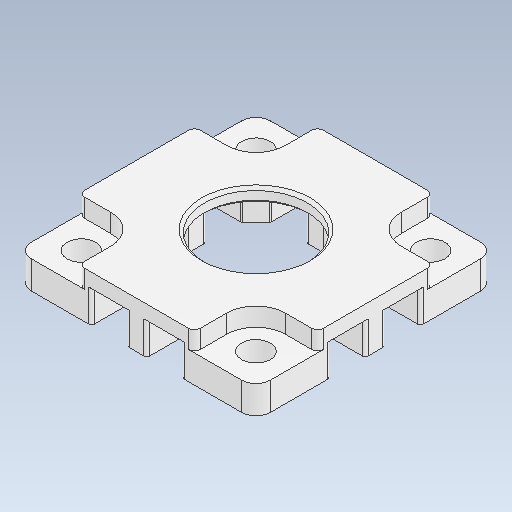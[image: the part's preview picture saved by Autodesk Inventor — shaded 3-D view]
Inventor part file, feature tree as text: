
AUTODESK INVENTOR PART (.ipt)
format: ipt  version: 2020 (Build 240168000, 168)  size: 182,784 bytes
history: native  units: in
note: dims shown in document units (in); Inventor stores cm internally (conversion verified against a paired STEP export)
features: fillet x1
ambient origin geometry x8: Origin, YZ Plane, XZ Plane, XY Plane, X Axis, Y Axis, Z Axis, Center Point
bodies: Solid1 (feature_tree)
feature tree (1):
  fillet  "Fillet4"  [1 undecoded]
note: 1 required parameter value undecoded (feature->parameter linkage not recoverable at this tier; creation-order binding heuristic only, values carry confidence <= 0.55)
